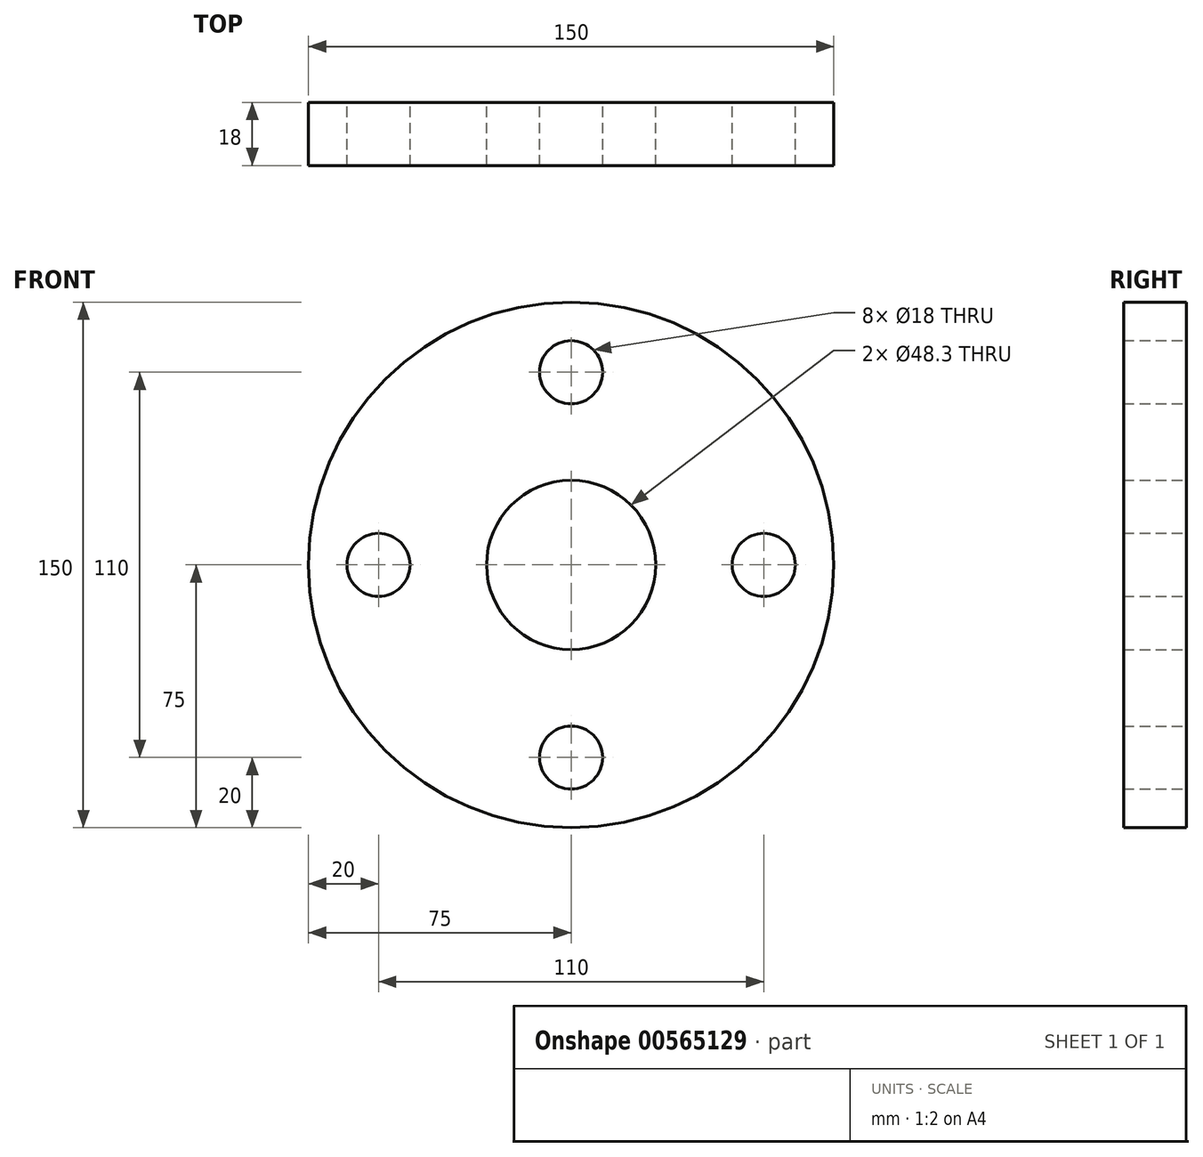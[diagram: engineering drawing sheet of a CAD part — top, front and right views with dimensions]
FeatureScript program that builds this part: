
annotation { "Feature Type Name" : "Feature", "Feature Type Description" : "" }
export const myFeature = defineFeature(function(context is Context, id is Id, definition is map)
    precondition{}
    {
        {
            var Q0;
            Q0=qCreatedBy(makeId("Front.planeOp"),FACE);
            var sketch = newSketch(context, id + "F0", { "sketchPlane" : qUnion([Q0])});
            skCircle(sketch, "E0", {"center": v(0, 0) * mm, "radius": 75 * mm});
            skCircle(sketch, "E1", {"center": v(0, 0) * mm, "radius": 24.15 * mm});
            skCircle(sketch, "E2", {"center": v(0, 0) * mm, "radius": 55 * mm, "construction": true});
            skCircle(sketch, "E3", {"center": v(0, 55) * mm, "radius": 9 * mm});
            skCircle(sketch, "E4", {"center": v(-55, 0) * mm, "radius": 9 * mm});
            skCircle(sketch, "E5", {"center": v(0, -55) * mm, "radius": 9 * mm});
            skCircle(sketch, "E6", {"center": v(55, 0) * mm, "radius": 9 * mm});
            skSolve(sketch);
        }
        {
            var Q0;
            Q0=makeQuery(id+"F0.imprint","IMPRINT",FACE,{"disambiguationData":[TD([[makeQuery(id+"F0.imprint","IMPRINT",EDGE,{"derivedFrom":sQuery(id+"F0.wireOp",EDGE,"E0")}),1.0]])]});
            extrude(context, id + "F1", {"entities" : qUnion([Q0]), "depth" : 18 * mm, "offsetDistance" : 25 * mm});
        }
        {
            var Q0;
            Q0=makeQuery(id+"F1.opExtrude","SWEPT_BODY",BODY,{"disambiguationData":[OSD([sQuery(id+"F0.wireOp",EDGE,"E0"),sQuery(id+"F0.wireOp",EDGE,"E1"),sQuery(id+"F0.wireOp",EDGE,"E3"),sQuery(id+"F0.wireOp",EDGE,"E4"),sQuery(id+"F0.wireOp",EDGE,"E5"),sQuery(id+"F0.wireOp",EDGE,"E6")])]});
            transform(context, id + "F2", {"entities" : qUnion([Q0]), "transformType" : TransformType.TRANSLATION_3D, "dx" : 0 * mm, "dy" : 0 * mm, "dz" : 0 * mm, "makeCopy" : true});
        }
    });
